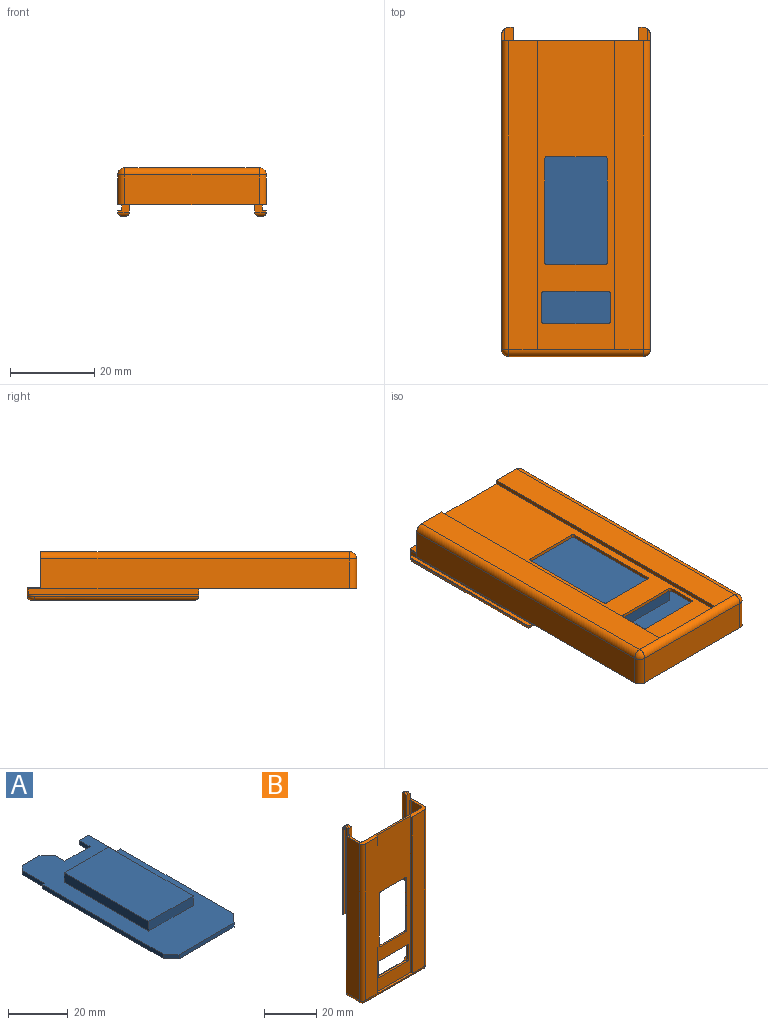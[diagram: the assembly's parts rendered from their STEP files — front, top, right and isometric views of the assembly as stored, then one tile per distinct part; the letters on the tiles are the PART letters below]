
ASSEMBLY  parts=2 mates=1
PART A: 23 faces, bbox 33.1x73.6x5.6 mm
  f0: plane 73.6x33.1mm, normal (0,0,1), area 1414.5mm2, adj f1,f2,f3,f4,f5,f6,f7,f8
  f1: plane 4x3.55mm, normal (0.75,-0.66,0), area 9.1mm2, adj f0,f2,f16,f17
  f2: plane 53x1.7mm, normal (1,0,0), area 90.1mm2, adj f0,f1,f3,f17
  f3: plane 2x1.7mm, normal (0,1,0), area 3.4mm2, adj f0,f2,f4,f17
  f4: plane 13.3x1.7mm, normal (1,0,0), area 22.6mm2, adj f0,f3,f5,f17
  f5: plane 4.3x1.7mm, normal (0,1,0), area 7.3mm2, adj f0,f4,f6,f17
  f6: plane 5x1.7mm, normal (-1,0,0), area 8.5mm2, adj f0,f5,f7,f17
  f7: plane 11.9x1.7mm, normal (0,1,0), area 20.2mm2, adj f0,f6,f8,f17
  f8: plane 4.3x1.7mm, normal (1,0,0), area 7.3mm2, adj f0,f7,f9,f17
  f9: plane 4x4mm, normal (0.71,0.71,0), area 9.6mm2, adj f0,f8,f10,f17
  f10: plane 8x1.7mm, normal (0,1,0), area 13.6mm2, adj f0,f9,f11,f17
  f11: plane 2x2mm, normal (-0.71,0.71,0), area 4.8mm2, adj f0,f10,f12,f17
  f12: plane 10.6x1.7mm, normal (-1,0,0), area 18mm2, adj f0,f11,f13,f17
  f13: plane 1.7x0.9mm, normal (0,1,0), area 1.5mm2, adj f0,f12,f14,f17
  f14: plane 57x1.7mm, normal (-1,0,0), area 96.9mm2, adj f0,f13,f15,f17
  f15: plane 4x3.55mm, normal (-0.75,-0.66,0), area 9.1mm2, adj f0,f14,f16,f17
  f16: plane 26x1.7mm, normal (0,-1,0), area 44.2mm2, adj f0,f1,f15,f17
  f17: plane 73.6x33.1mm, normal (0,0,-1), area 2254.5mm2, adj f1,f2,f3,f4,f5,f6,f7,f8
  f18: plane 21x3.9mm, normal (0,-1,0), area 81.9mm2, adj f0,f19,f21,f22
  f19: plane 40x3.9mm, normal (1,0,0), area 156mm2, adj f0,f18,f20,f22
  f20: plane 21x3.9mm, normal (0,1,0), area 81.9mm2, adj f0,f19,f21,f22
  f21: plane 40x3.9mm, normal (-1,0,0), area 156mm2, adj f0,f18,f20,f22
  f22: plane 40x21mm, normal (0,0,1), area 840mm2, adj f18,f19,f20,f21
PART B: 93 faces, bbox 35.3x11.5x78.1 mm
  f0: plane 38.65x0.8mm, normal (0,1,0), area 30.8mm2, adj f70,f71,f72,f73,f92
  f1: plane 38.65x0.8mm, normal (0,1,0), area 30.8mm2, adj f66,f67,f68,f69,f90
  f2: plane 3.34x2.2mm, normal (0,0,1), area 7.3mm2, adj f14,f40,f41,f75,f77
  f3: plane 30x2mm, normal (0,-1,0), area 35.8mm2, adj f16,f18,f57,f64,f76,f77,f91
  f4: plane 73.2x31.9mm, normal (0,1,0), area 1662.1mm2, adj f18,f19,f20,f21,f22,f23,f24,f25
  f5: plane 30x2mm, normal (0,-1,0), area 35.8mm2, adj f18,f36,f59,f65,f87,f88,f89
  f6: plane 3.05x1.8mm, normal (0,0,1), area 5.5mm2, adj f8,f15,f74,f79
  f7: plane 46.2x3.34mm, normal (0,-1,0), area 84.4mm2, adj f17,f36,f39,f87,f88
  f8: plane 46.2x3.34mm, normal (0,1,0), area 84.5mm2, adj f6,f15,f17,f39,f74
  f9: plane 73.2x7.1mm, normal (1,0,0), area 519.7mm2, adj f12,f18,f46,f48
  f10: plane 73.2x7.1mm, normal (-1,0,0), area 519.7mm2, adj f12,f18,f42,f43
  f11: plane 2.8x1.7mm, normal (0,0,-1), area 3.4mm2, adj f12,f16,f28,f62,f63,f73
  f12: plane 77.95x35.3mm, normal (0,1,0), area 317.6mm2, adj f9,f10,f11,f14,f16,f17,f18,f27
  f13: plane 73.2x6.75mm, normal (0,-1,0), area 494.1mm2, adj f18,f33,f45,f46
  f14: plane 6.3x1.93mm, normal (-0.75,0,0.66), area 11.2mm2, adj f2,f12,f16,f35,f38,f40,f41,f83
  f15: plane 44.47x3.05mm, normal (1,0,0), area 135.6mm2, adj f6,f8,f17,f80
  f16: plane 75.17x2.75mm, normal (-1,0,0), area 128.2mm2, adj f3,f11,f12,f14,f40,f57,f72,f76
  f17: plane 6.3x1.93mm, normal (0.75,0,0.66), area 11.2mm2, adj f7,f8,f12,f15,f35,f36,f39,f81
  f18: plane 35.3x8.8mm, normal (0,0,1), area 58.2mm2, adj f3,f4,f5,f9,f10,f12,f13,f30
  f19: plane 24.6x0.8mm, normal (-1,0,0), area 19.7mm2, adj f4,f34,f53,f56
  f20: plane 13.8x0.8mm, normal (0,0,1), area 11mm2, adj f4,f34,f53,f54
  f21: plane 24.6x0.8mm, normal (1,0,0), area 19.7mm2, adj f4,f34,f54,f55
  f22: plane 6.7x0.8mm, normal (-1,0,0), area 5.4mm2, adj f4,f34,f49,f52
  f23: plane 15.3x0.8mm, normal (0,0,1), area 12.2mm2, adj f4,f34,f49,f50
  f24: plane 6.7x0.8mm, normal (1,0,0), area 5.4mm2, adj f4,f34,f50,f51
  f25: plane 13.8x0.8mm, normal (0,0,-1), area 11mm2, adj f4,f34,f55,f56
  f26: plane 15.3x0.8mm, normal (0,0,-1), area 12.2mm2, adj f4,f34,f51,f52
  f27: plane 31.9x7.1mm, normal (0,0,-1), area 226.5mm2, adj f12,f42,f45,f48
  f28: plane 38.95x0.35mm, normal (1,0,0), area 13.6mm2, adj f11,f63,f71,f91
  f29: plane 38.95x0.35mm, normal (-1,0,0), area 13.6mm2, adj f58,f60,f66,f89
  f30: plane 73.2x6.75mm, normal (0,-1,0), area 494.1mm2, adj f18,f31,f43,f45
  f31: plane 73.2x1mm, normal (1,0,0), area 73.2mm2, adj f18,f30,f32,f34
  f32: plane 18.4x1mm, normal (0,0,1), area 18.4mm2, adj f31,f33,f34,f45
  f33: plane 73.2x1mm, normal (-1,0,0), area 73.2mm2, adj f13,f18,f32,f34
  f34: plane 73.2x18.4mm, normal (0,-1,0), area 842.9mm2, adj f18,f19,f20,f21,f22,f23,f24,f25
  f35: plane 26.27x6.3mm, normal (0,0,1), area 165.5mm2, adj f12,f14,f17,f82
  f36: plane 75.17x2.75mm, normal (1,0,0), area 128.2mm2, adj f5,f7,f12,f17,f58,f59,f69,f87
  f37: plane 3.05x1.8mm, normal (0,0,1), area 5.5mm2, adj f38,f41,f75,f85
  f38: plane 44.47x3.05mm, normal (-1,0,0), area 135.6mm2, adj f14,f37,f41,f84
  f39: plane 3.34x2.2mm, normal (0,0,1), area 7.3mm2, adj f7,f8,f17,f74,f88
  f40: plane 46.2x3.34mm, normal (0,-1,0), area 84.4mm2, adj f2,f14,f16,f76,f77
  f41: plane 46.2x3.34mm, normal (0,1,0), area 84.5mm2, adj f2,f14,f37,f38,f75
  f42: cylinder r=1.7mm len=7.1mm, axis (0,1,0), area 19mm2, adj f10,f12,f27,f44
  f43: cylinder r=1.7mm len=73.2mm, axis (0,0,1), area 195.5mm2, adj f10,f18,f30,f44
  f44: sphere r=1.7mm, area 4.5mm2, adj f42,f43,f45
  f45: cylinder r=1.7mm len=31.9mm, axis (-1,0,0), area 85.2mm2, adj f13,f27,f30,f32,f44,f47
  f46: cylinder r=1.7mm len=73.2mm, axis (0,0,-1), area 195.5mm2, adj f9,f13,f18,f47
  f47: sphere r=1.7mm, area 4.5mm2, adj f45,f46,f48
  f48: cylinder r=1.7mm len=7.1mm, axis (0,-1,0), area 19mm2, adj f9,f12,f27,f47
  f49: cylinder r=0.5mm len=0.8mm, axis (0,1,0), area 0.6mm2, adj f4,f22,f23,f34
  f50: cylinder r=0.5mm len=0.8mm, axis (0,-1,0), area 0.6mm2, adj f4,f23,f24,f34
  f51: cylinder r=0.5mm len=0.8mm, axis (0,1,0), area 0.6mm2, adj f4,f24,f26,f34
  f52: cylinder r=0.5mm len=0.8mm, axis (0,-1,0), area 0.6mm2, adj f4,f22,f26,f34
  f53: cylinder r=0.5mm len=0.8mm, axis (0,1,0), area 0.6mm2, adj f4,f19,f20,f34
  f54: cylinder r=0.5mm len=0.8mm, axis (0,-1,0), area 0.6mm2, adj f4,f20,f21,f34
  f55: cylinder r=0.5mm len=0.8mm, axis (0,1,0), area 0.6mm2, adj f4,f21,f25,f34
  f56: cylinder r=0.5mm len=0.8mm, axis (0,-1,0), area 0.6mm2, adj f4,f19,f25,f34
  f57: plane 2.1x1.1mm, normal (0,0,1), area 2.3mm2, adj f3,f16,f70,f91
  f58: plane 2.8x1.7mm, normal (0,0,-1), area 3.4mm2, adj f12,f29,f36,f60,f61,f67
  f59: plane 2.1x1.1mm, normal (0,0,1), area 2.3mm2, adj f5,f36,f68,f89
  f60: plane 40.5x1mm, normal (0,-1,0), area 40.1mm2, adj f29,f58,f61,f89
  f61: plane 40.5x1.35mm, normal (-1,0,0), area 54.7mm2, adj f12,f58,f60,f89
  f62: plane 40.5x1.35mm, normal (1,0,0), area 54.7mm2, adj f11,f12,f63,f91
  f63: plane 40.5x1mm, normal (0,-1,0), area 40.1mm2, adj f11,f28,f62,f91
  f64: plane 2.94x0.4mm, normal (1,0,0), area 1.2mm2, adj f3,f12,f18,f91
  f65: plane 2.94x0.4mm, normal (-1,0,0), area 1.2mm2, adj f5,f12,f18,f89
  f66: cylinder r=1mm len=38.95mm, axis (0,0,1), area 60.6mm2, adj f1,f29,f67,f90
  f67: cylinder r=1mm len=2.8mm, axis (1,0,0), area 3.3mm2, adj f1,f58,f66,f69
  f68: cylinder r=1mm len=1.1mm, axis (-1,0,0), area 1.2mm2, adj f1,f59,f69,f90
  f69: cylinder r=1mm len=40.65mm, axis (0,0,-1), area 62.7mm2, adj f1,f36,f67,f68
  f70: cylinder r=1mm len=1.1mm, axis (-1,0,0), area 1.2mm2, adj f0,f57,f72,f92
  f71: cylinder r=1mm len=38.95mm, axis (0,0,-1), area 60.6mm2, adj f0,f28,f73,f92
  f72: cylinder r=1mm len=40.65mm, axis (0,0,-1), area 62.7mm2, adj f0,f16,f70,f73
  f73: cylinder r=1mm len=2.8mm, axis (1,0,0), area 3.3mm2, adj f0,f11,f71,f72
  f74: plane 73.7x5.2mm, normal (1,0,0), area 242.3mm2, adj f6,f8,f18,f39,f78,f88
  f75: plane 73.7x5.2mm, normal (-1,0,0), area 242.3mm2, adj f2,f18,f37,f41,f77,f86
  f76: cylinder r=0.7mm len=1.8mm, axis (1,0,0), area 1.6mm2, adj f3,f16,f40,f77
  f77: cylinder r=0.7mm len=73.7mm, axis (0,0,-1), area 32.3mm2, adj f2,f3,f18,f40,f75,f76
  f78: cylinder r=0.7mm len=27.5mm, axis (0,0,-1), area 30mm2, adj f4,f18,f74,f79
  f79: cylinder r=0.7mm len=2.5mm, axis (-1,0,0), area 2mm2, adj f4,f6,f78,f80
  f80: cylinder r=0.7mm len=45.17mm, axis (0,0,1), area 49.1mm2, adj f4,f15,f79,f81
  f81: cylinder r=0.7mm len=2.4mm, axis (0.66,0,-0.75), area 2.6mm2, adj f4,f17,f80,f82
  f82: cylinder r=0.7mm len=26.27mm, axis (1,0,0), area 28.6mm2, adj f4,f35,f81,f83
  f83: cylinder r=0.7mm len=2.4mm, axis (0.66,0,0.75), area 2.6mm2, adj f4,f14,f82,f84
  f84: cylinder r=0.7mm len=45.17mm, axis (0,0,-1), area 49.1mm2, adj f4,f38,f83,f85
  f85: cylinder r=0.7mm len=2.5mm, axis (-1,0,0), area 2mm2, adj f4,f37,f84,f86
  f86: cylinder r=0.7mm len=27.5mm, axis (0,0,1), area 30mm2, adj f4,f18,f75,f85
  f87: cylinder r=0.7mm len=1.8mm, axis (1,0,0), area 1.6mm2, adj f5,f7,f36,f88
  f88: cylinder r=0.7mm len=73.7mm, axis (0,0,1), area 32.3mm2, adj f5,f7,f18,f39,f74,f87
  f89: cylinder r=1.7mm len=2.1mm, axis (0,-1,0), area 2.3mm2, adj f5,f12,f29,f59,f60,f61,f65,f90
  f90: torus R=0.7mm, axis (0,1,0), area 3.3mm2, adj f1,f66,f68,f89
  f91: cylinder r=1.7mm len=2.1mm, axis (0,-1,0), area 2.3mm2, adj f3,f12,f28,f57,f62,f63,f64,f92
  f92: torus R=0.7mm, axis (0,1,0), area 3.3mm2, adj f0,f70,f71,f91
PLACE A t=(-4.26,-44.46,26.95)mm
PLACE B rot(axis=(-1,0,0),90deg) t=(-4.26,-45.11,26.95)mm
MATE fastened A.f17 <-> B.f12  axis (0,0,-1) through (-4.26,-81.26,26.95)mm
